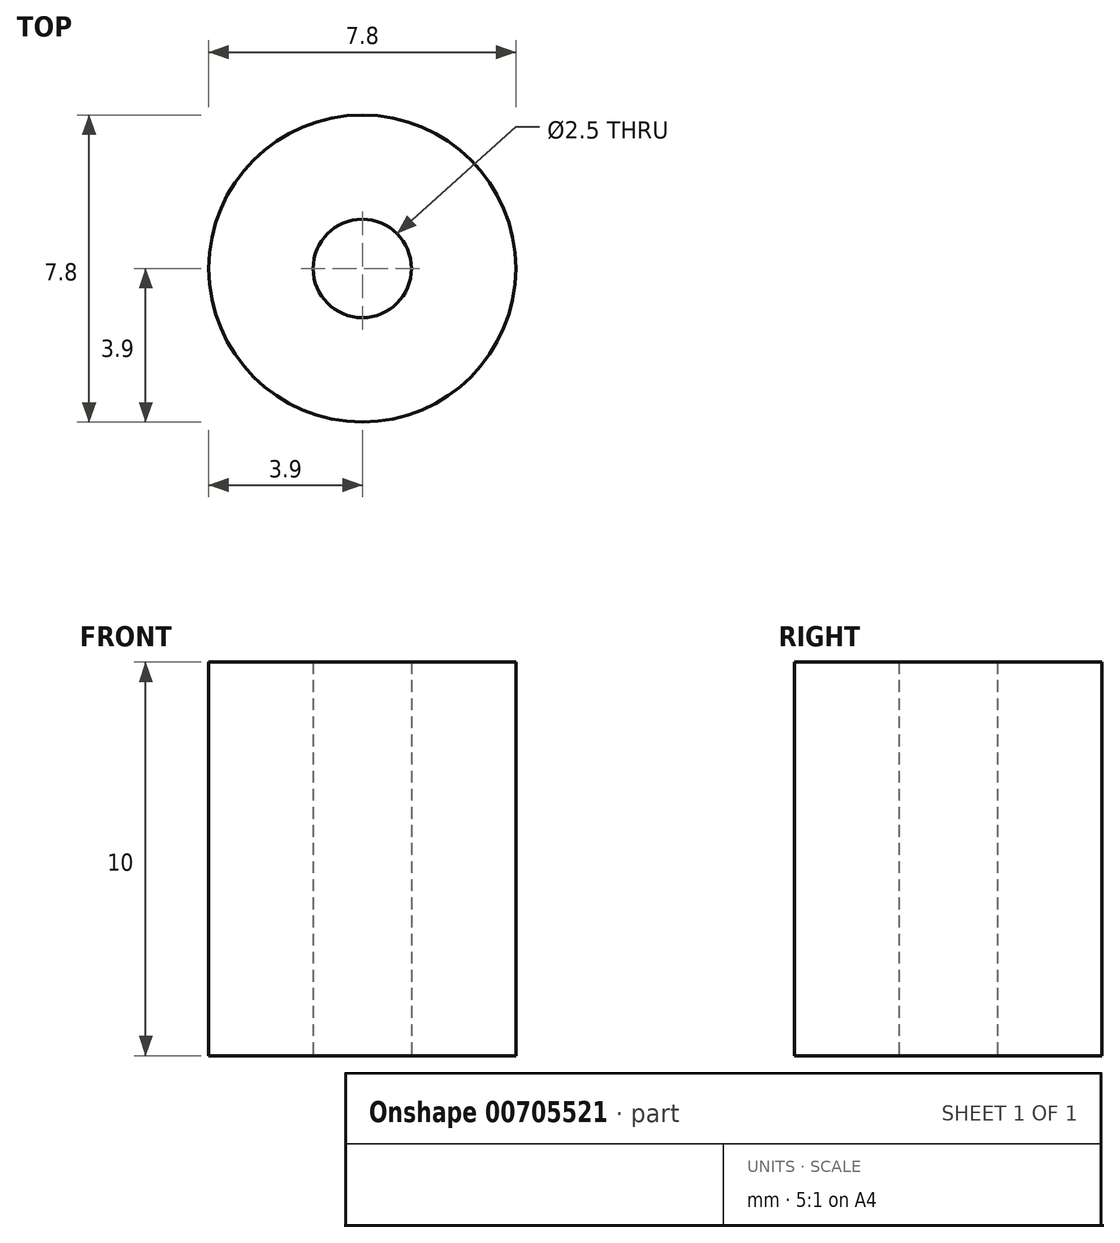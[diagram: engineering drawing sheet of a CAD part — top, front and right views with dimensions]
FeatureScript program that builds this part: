
annotation { "Feature Type Name" : "Feature", "Feature Type Description" : "" }
export const myFeature = defineFeature(function(context is Context, id is Id, definition is map)
    precondition{}
    {
        {
            var Q0;
            Q0=qCreatedBy(makeId("Top.planeOp"),FACE);
            var sketch = newSketch(context, id + "F0", { "sketchPlane" : qUnion([Q0])});
            skCircle(sketch, "E0", {"center": v(0, 0) * mm, "radius": 1.25 * mm});
            skCircle(sketch, "E1", {"center": v(0, 0) * mm, "radius": 3.9 * mm});
            skSolve(sketch);
        }
        {
            var Q0;
            Q0=makeQuery(id+"F0.imprint","IMPRINT",FACE,{"disambiguationData":[TD([[makeQuery(id+"F0.imprint","IMPRINT",EDGE,{"derivedFrom":sQuery(id+"F0.wireOp",EDGE,"E0")}),-1.0]])]});
            extrude(context, id + "F1", {"entities" : qUnion([Q0]), "depth" : 10 * mm, "offsetDistance" : 25.4 * mm});
        }
    });
